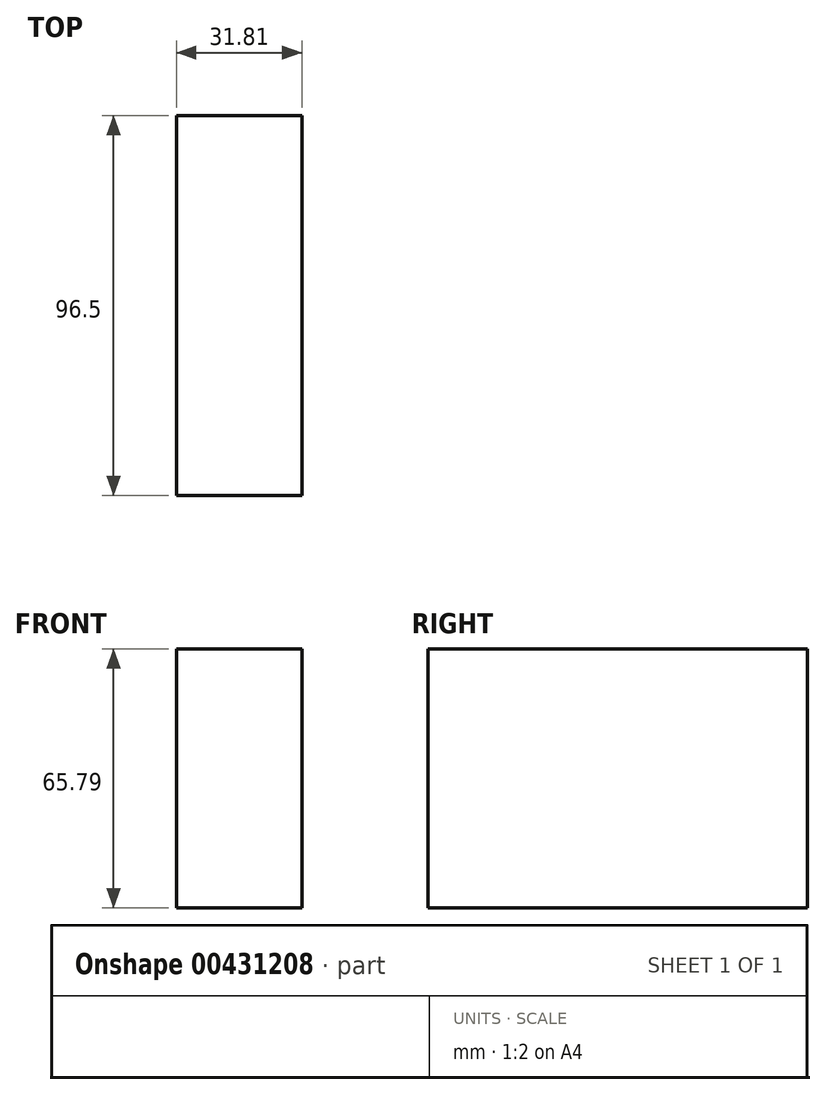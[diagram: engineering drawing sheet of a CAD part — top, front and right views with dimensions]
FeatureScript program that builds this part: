
annotation { "Feature Type Name" : "Feature", "Feature Type Description" : "" }
export const myFeature = defineFeature(function(context is Context, id is Id, definition is map)
    precondition{}
    {
        {
            var Q0;
            Q0=qCreatedBy(makeId("Top.planeOp"),FACE);
            var sketch = newSketch(context, id + "F0", { "sketchPlane" : qUnion([Q0])});
            skLineSegment(sketch, "E0.bottom", {"start": v(-62.26, 61.02) * mm, "end": v(62.13, 61.02) * mm});
            skLineSegment(sketch, "E0.top", {"start": v(-62.26, -62.6) * mm, "end": v(62.13, -62.6) * mm});
            skLineSegment(sketch, "E0.left", {"start": v(-62.26, 61.02) * mm, "end": v(-62.26, -62.6) * mm});
            skLineSegment(sketch, "E0.right", {"start": v(62.13, 61.02) * mm, "end": v(62.13, -62.6) * mm});
            skSolve(sketch);
        }
        {
            var Q0;
            Q0=makeQuery(id+"F0.imprint","IMPRINT",FACE,{"disambiguationData":[TD([[makeQuery(id+"F0.imprint","IMPRINT",EDGE,{"derivedFrom":sQuery(id+"F0.wireOp",EDGE,"E0.bottom")}),-1.0]])]});
            var sketch = newSketch(context, id + "F1", { "sketchPlane" : qUnion([Q0])});
            skLineSegment(sketch, "E1.bottom", {"start": v(-27.27, 45.87) * mm, "end": v(4.54, 45.87) * mm});
            skLineSegment(sketch, "E1.top", {"start": v(-27.27, -50.63) * mm, "end": v(4.54, -50.63) * mm});
            skLineSegment(sketch, "E1.left", {"start": v(-27.27, 45.87) * mm, "end": v(-27.27, -50.63) * mm});
            skLineSegment(sketch, "E1.right", {"start": v(4.54, 45.87) * mm, "end": v(4.54, -50.63) * mm});
            skSolve(sketch);
        }
        {
            var Q0;
            Q0=makeQuery(id+"F1.imprint","IMPRINT",FACE,{"disambiguationData":[TD([[makeQuery(id+"F1.imprint","IMPRINT",EDGE,{"derivedFrom":sQuery(id+"F1.wireOp",EDGE,"E1.bottom")}),-1.0]])]});
            extrude(context, id + "F2", {"entities" : qUnion([Q0]), "depth" : 65.8 * mm});
        }
    });
